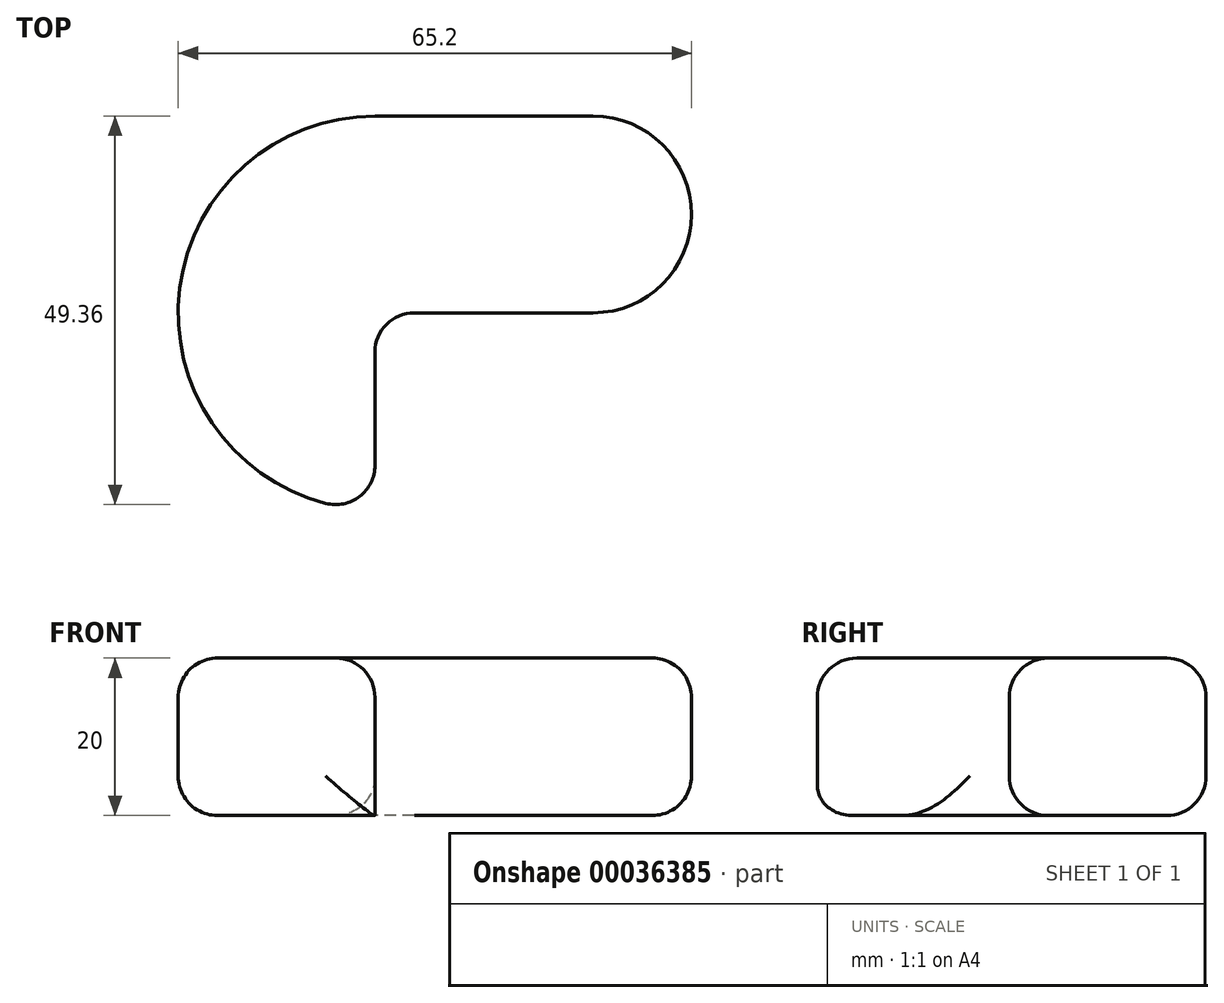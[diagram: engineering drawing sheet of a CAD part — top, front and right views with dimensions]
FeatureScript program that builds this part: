
annotation { "Feature Type Name" : "Feature", "Feature Type Description" : "" }
export const myFeature = defineFeature(function(context is Context, id is Id, definition is map)
    precondition{}
    {
        {
            var Q0;
            Q0=qCreatedBy(makeId("Top.planeOp"),FACE);
            var sketch = newSketch(context, id + "F0", { "sketchPlane" : qUnion([Q0])});
            skLineSegment(sketch, "E0.bottom", {"start": v(-18, 50) * mm, "end": v(9.7, 50) * mm});
            skLineSegment(sketch, "E0.top", {"start": v(-18, 25) * mm, "end": v(9.7, 25) * mm});
            skLineSegment(sketch, "E0.left", {"start": v(-18, 50) * mm, "end": v(-18, 25) * mm});
            skLineSegment(sketch, "E0.right", {"start": v(9.7, 50) * mm, "end": v(9.7, 25) * mm});
            skArc(sketch, "E1", {"start": v(-18, 50) * mm, "mid": v(-43, 25) * mm, "end": v(-18, 0) * mm});
            skLineSegment(sketch, "E2", {"start": v(-18, 0) * mm, "end": v(-18, 25) * mm});
            skArc(sketch, "E3", {"start": v(9.7, 25) * mm, "mid": v(22.2, 37.5) * mm, "end": v(9.7, 50) * mm});
            skSolve(sketch);
        }
        {
            var Q0;
            {var subQ0=sQuery(id+"F0.wireOp",EDGE,"1c7c6869-84e6-4fa8-a150-36d2dfb50124");Q0=makeQuery(id+"F0.imprint","IMPRINT",FACE,{"disambiguationData":[TD([[makeQuery(id+"F0.imprint","IMPRINT",EDGE,{"derivedFrom":subQ0}),-1.0]])]});}
            var Q1;
            {var subQ0=sQuery(id+"F0.wireOp",EDGE,"0e4b8667-bdd4-42b6-903c-a061d0090455");Q1=makeQuery(id+"F0.imprint","IMPRINT",FACE,{"disambiguationData":[TD([[makeQuery(id+"F0.imprint","IMPRINT",EDGE,{"derivedFrom":subQ0}),1.0]])]});}
            var Q2;
            Q2=makeQuery(id+"F0.imprint","IMPRINT",FACE,{"disambiguationData":[TD([[makeQuery(id+"F0.imprint","IMPRINT",EDGE,{"derivedFrom":sQuery(id+"F0.wireOp",EDGE,"E0.left")}),-1.0]])]});
            var Q3;
            Q3=makeQuery(id+"F0.imprint","IMPRINT",FACE,{"disambiguationData":[TD([[makeQuery(id+"F0.imprint","IMPRINT",EDGE,{"derivedFrom":sQuery(id+"F0.wireOp",EDGE,"E0.right")}),1.0]])]});
            var Q4;
            Q4=makeQuery(id+"F0.imprint","IMPRINT",FACE,{"disambiguationData":[TD([[makeQuery(id+"F0.imprint","IMPRINT",EDGE,{"derivedFrom":sQuery(id+"F0.wireOp",EDGE,"E0.bottom")}),-1.0]])]});
            extrude(context, id + "F1", {"entities" : qUnion([Q0, Q1, Q2, Q3, Q4]), "depth" : 10 * mm});
        }
        {
            var Q0;
            Q0=makeQuery(id+"F1.opExtrude","CAP_FACE",FACE,{"disambiguationData":[OSD([sQuery(id+"F0.wireOp",EDGE,"E0.top"),sQuery(id+"F0.wireOp",EDGE,"E0.left"),sQuery(id+"F0.wireOp",EDGE,"E0.right"),sQuery(id+"F0.wireOp",EDGE,"1c7c6869-84e6-4fa8-a150-36d2dfb50124"),sQuery(id+"F0.wireOp",EDGE,"0e4b8667-bdd4-42b6-903c-a061d0090455")])],"isStart":false});
            extrude(context, id + "F2", {"entities" : qUnion([Q0]), "operationType" : NewBodyOperationType.ADD, "depth" : 10 * mm});
        }
        {
            var Q0;
            Q0=makeQuery(id+"F2.opExtrude","CAP_EDGE",EDGE,{"disambiguationData":[OSD([sQuery(id+"F0.wireOp",EDGE,"E0.top")])],"isStart":false});
            var Q1;
            Q1=makeQuery(id+"F2.opExtrude","CAP_EDGE",EDGE,{"disambiguationData":[OSD([sQuery(id+"F0.wireOp",EDGE,"1c7c6869-84e6-4fa8-a150-36d2dfb50124")])],"isStart":false});
            var Q2;
            Q2=makeQuery(id+"F2.opExtrude","CAP_EDGE",EDGE,{"disambiguationData":[OSD([sQuery(id+"F0.wireOp",EDGE,"0e4b8667-bdd4-42b6-903c-a061d0090455")])],"isStart":false});
            var Q3;
            Q3=makeQuery(id+"F2.opExtrude","CAP_EDGE",EDGE,{"disambiguationData":[OSD([sQuery(id+"F0.wireOp",EDGE,"E0.left")])],"isStart":false});
            var Q4;
            Q4=makeQuery(id+"F2.opExtrude","CAP_EDGE",EDGE,{"disambiguationData":[OSD([sQuery(id+"F0.wireOp",EDGE,"E0.right")])],"isStart":false});
            var Q5;
            {var subQ0=sQuery(id+"F0.wireOp",EDGE,"E0.top");var subQ1=sQuery(id+"F0.wireOp",EDGE,"E0.right");Q5=makeQuery(id+"F2.boolean.opBoolean","MERGE",EDGE,{"derivedFrom":[makeQuery(id+"F1.opExtrude","SWEPT_EDGE",EDGE,{"disambiguationData":[OSD([subQ0,subQ1])]}),makeQuery(id+"F2.opExtrude","SWEPT_EDGE",EDGE,{"disambiguationData":[OSD([subQ0,subQ1])]})]});}
            var Q6;
            Q6=makeQuery(id+"F1.opExtrude","CAP_EDGE",EDGE,{"disambiguationData":[OSD([sQuery(id+"F0.wireOp",EDGE,"E0.top")])],"isStart":true});
            var Q7;
            {var subQ0=sQuery(id+"F0.wireOp",EDGE,"E0.top");var subQ1=sQuery(id+"F0.wireOp",EDGE,"E0.left");Q7=makeQuery(id+"F2.boolean.opBoolean","MERGE",EDGE,{"derivedFrom":[makeQuery(id+"F1.opExtrude","SWEPT_EDGE",EDGE,{"disambiguationData":[OSD([subQ0,subQ1])]}),makeQuery(id+"F2.opExtrude","SWEPT_EDGE",EDGE,{"disambiguationData":[OSD([subQ0,subQ1])]})]});}
            var Q8;
            Q8=makeQuery(id+"F1.opExtrude","CAP_EDGE",EDGE,{"disambiguationData":[OSD([sQuery(id+"F0.wireOp",EDGE,"E0.left")])],"isStart":true});
            var Q9;
            Q9=makeQuery(id+"F1.opExtrude","CAP_EDGE",EDGE,{"disambiguationData":[OSD([sQuery(id+"F0.wireOp",EDGE,"1c7c6869-84e6-4fa8-a150-36d2dfb50124")])],"isStart":true});
            var Q10;
            Q10=makeQuery(id+"F1.opExtrude","CAP_EDGE",EDGE,{"disambiguationData":[OSD([sQuery(id+"F0.wireOp",EDGE,"0e4b8667-bdd4-42b6-903c-a061d0090455")])],"isStart":true});
            var Q11;
            Q11=makeQuery(id+"F1.opExtrude","CAP_EDGE",EDGE,{"disambiguationData":[OSD([sQuery(id+"F0.wireOp",EDGE,"E0.right")])],"isStart":true});
            var Q12;
            {var subQ0=sQuery(id+"F0.wireOp",EDGE,"E0.bottom");var subQ1=sQuery(id+"F0.wireOp",EDGE,"1c7c6869-84e6-4fa8-a150-36d2dfb50124");var subQ2=sQuery(id+"F0.wireOp",EDGE,"0e4b8667-bdd4-42b6-903c-a061d0090455");Q12=makeQuery(id+"F2.boolean.opBoolean","MERGE",EDGE,{"derivedFrom":[makeQuery(id+"F1.opExtrude","SWEPT_EDGE",EDGE,{"disambiguationData":[OSD([subQ0,subQ1,subQ2])]}),makeQuery(id+"F2.opExtrude","SWEPT_EDGE",EDGE,{"disambiguationData":[OSD([subQ0,subQ1,subQ2])]})]});}
            var Q13;
            Q13=makeQuery(id+"F2.opExtrude","CAP_EDGE",EDGE,{"disambiguationData":[OSD([sQuery(id+"F0.wireOp",EDGE,"E0.bottom")])],"isStart":false});
            var Q14;
            Q14=makeQuery(id+"F2.opExtrude","CAP_EDGE",EDGE,{"disambiguationData":[OSD([sQuery(id+"F0.wireOp",EDGE,"E3")])],"isStart":false});
            var Q15;
            Q15=makeQuery(id+"F2.opExtrude","CAP_EDGE",EDGE,{"disambiguationData":[OSD([sQuery(id+"F0.wireOp",EDGE,"E1")])],"isStart":false});
            var Q16;
            Q16=makeQuery(id+"F2.opExtrude","CAP_EDGE",EDGE,{"disambiguationData":[OSD([sQuery(id+"F0.wireOp",EDGE,"E2")])],"isStart":false});
            var Q17;
            {var subQ0=sQuery(id+"F0.wireOp",EDGE,"E1");Q17=makeQuery(id+"F2.boolean.opBoolean","MERGE",FACE,{"derivedFrom":[makeQuery(id+"F1.opExtrude","SWEPT_FACE",FACE,{"disambiguationData":[OSD([subQ0])]}),makeQuery(id+"F2.opExtrude","SWEPT_FACE",FACE,{"disambiguationData":[OSD([subQ0])]})]});}
            var Q18;
            Q18=makeQuery(id+"F1.opExtrude","CAP_EDGE",EDGE,{"disambiguationData":[OSD([sQuery(id+"F0.wireOp",EDGE,"E1")])],"isStart":true});
            fillet(context, id + "F3", {"entities" : qUnion([Q0, Q1, Q2, Q3, Q4, Q5, Q6, Q7, Q8, Q9, Q10, Q11, Q12, Q13, Q14, Q15, Q16, Q17, Q18]), "radius" : 5 * mm, "tangentPropagation" : true, "allowEdgeOverflow" : false});
        }
    });
